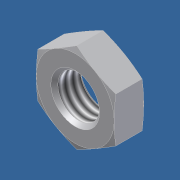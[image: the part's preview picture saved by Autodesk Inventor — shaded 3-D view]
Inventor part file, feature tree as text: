
AUTODESK INVENTOR PART (.ipt)
format: ipt  version: 2012 (Build 160160000, 160)  size: 130,048 bytes
history: native  units: in
note: dims shown in document units (in); Inventor stores cm internally (conversion verified against a paired STEP export)
features: other x70, sketch x3, revolve x2, extrude x1, thread x1
ambient origin geometry x8: Origin, YZ Plane, XZ Plane, XY Plane, X Axis, Y Axis, Z Axis, Center Point
bodies: Solid1 (feature_tree)
feature tree (77):
  sketch  "Sketch_8"  dims[d0=360.0deg d1=0.19in d2=0.0in]
  sketch  "Sketch_10"  dims[d3=360.0deg d4=0.19in d5=0.0in]
  revolve  "Revolution1"  [1 undecoded]
  extrude  "Extrusion1"  Depth=0.19in TaperAngle=0.0deg
  revolve  "Revolution2"  [1 undecoded]
  thread  "Thread1"  [1 undecoded]
  other  "NUT_XY"
  other  "NUT_YZ"
  other  "NUT_ZX"
  other  "NUT_X"
  other  "NUT_Y"
  other  "NUT_Z"
  other  "NUT_Center"
  other  "a1_XY"
  other  "a1_YZ"
  other  "a1_ZX"
  other  "a1_X"
  other  "a1_Y"
  other  "a1_Z"
  other  "a1_Center"
  other  "a2_XY"
  other  "a2_YZ"
  other  "a2_ZX"
  other  "a2_X"
  other  "a2_Y"
  other  "a2_Z"
  other  "a2_Center"
  other  "b1_XY"
  other  "b1_YZ"
  other  "b1_ZX"
  other  "b1_X"
  other  "b1_Y"
  other  "b1_Z"
  other  "b1_Center"
  other  "b2_XY"
  other  "b2_YZ"
  other  "b2_ZX"
  other  "b2_X"
  other  "b2_Y"
  other  "b2_Z"
  other  "b2_Center"
  other  "e_XY"
  other  "e_YZ"
  other  "e_ZX"
  other  "e_X"
  other  "e_Y"
  other  "e_Z"
  other  "e_Center"
  other  "th1_XY"
  other  "th1_YZ"
  other  "th1_ZX"
  other  "th1_X"
  other  "th1_Y"
  other  "th1_Z"
  other  "th1_Center"
  other  "th2_XY"
  other  "th2_YZ"
  other  "th2_ZX"
  other  "th2_X"
  other  "th2_Y"
  other  "th2_Z"
  other  "th2_Center"
  other  "ol1_XY"
  other  "ol1_YZ"
  other  "ol1_ZX"
  other  "ol1_X"
  other  "ol1_Y"
  other  "ol1_Z"
  other  "ol1_Center"
  other  "ol2_XY"
  other  "ol2_YZ"
  other  "ol2_ZX"
  other  "ol2_X"
  other  "ol2_Y"
  other  "ol2_Z"
  other  "ol2_Center"
  sketch  "Sketch_11"
note: 3 required parameter values undecoded (feature->parameter linkage not recoverable at this tier; creation-order binding heuristic only, values carry confidence <= 0.55)